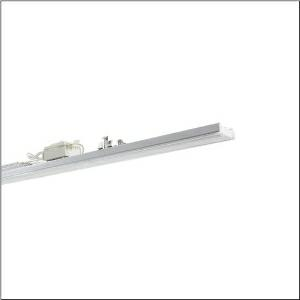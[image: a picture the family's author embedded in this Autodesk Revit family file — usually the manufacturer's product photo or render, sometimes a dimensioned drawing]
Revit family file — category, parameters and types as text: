
# Revit family: licross_r__21_recessed_ho_52tl12mn4fxm_f100
name_source: partatom
category: Lighting Fixtures
units: mm (PartAtom-declared; Revit-internal decimal feet)

## family parameters
Cut with Voids When Loaded = No
Host = Face
Light Source = No
Part Type = Normal
Room Calculation Point = No
Round Connector Dimension = Use Diameter
Shared = No

## types (1)
- --- (1 x LED, 15100 lm, 83.1 W, 4000K)
    Apparent Load = 83 VA
    CIE Flux Codes = 69 91 98 100 100
    Color Rendering = 80
    Color Temperature = 4000K
    Default Elevation = 1800 mm
    Description = Licross® 21 Recessed HO, luminaire insert, of sheet steel, galvanised, coil coated, white, length: 1.500mm, width: 66mm, height: 67mm, LED rated luminous flux: 15.100lm, light colour: 840, control gear: ON/OFF Multilumen, with plug, 3-pole, with phase selection, mains connection: 220..240V, AC, 50/60Hz, rated input power: 83W, halogen-free wiring, primary optical cover: cover, of PMMA, light emission: direct distribution, primary light characteristic: symmetric, protection rating (complete): IP40, insulation class (complete): insulation class I (protective earthing), certification: CE, ENEC, VDE, UKCA, protection symbol: D if used in an environment without relevant dust loads with corresponding accessories, impact resistance: IK06, permissible ambient temperature for indoor applications: -35..+30°C, corresponds to IFS (International Featured Standards) requirements for safety and quality in the food industry, reducing of maximum allowable ambient temperature of 5°C with ceiling mounting, LABS conformity tested according to VDMA 24364:2018-05, packaging unit: 1 piece
    Height = 58 mm
    Lamp = 1 x LED
    Lamp Light Flux = 15100 lm
    Lamp Power = 83.1 W
    Lamp count = 1
    Length = 1500 mm
    Luminous efficacy = 182 lm/W
    Manufacturer = Siteco
    ModVariant = No
    Model = 52TL12MN4FXM
    Mounting Place = Ceiling
    Mounting Type = Pendant
    Number of Poles = 1
    OnlyDefault = Yes
    Power Factor = 1
    Product Name = Licross® 21 Recessed HO
    Product group = luminaire insert
    ProductGroupID = 902
    Protection Class = Protection class I
    Protection Degree = IP 40
    RLX_Detail_Level = 1
    RLX_Emergency_Light_Flux = 0 lm
    RLX_Emergency_Type = 0
    RLX_Emergency_Type_DB = No
    RlxData = <blob elided: 22329 chars, md5=3d23784e>
    Socket = socket
    Standby Power = 0 W
    System Light Flux = 15100 lm
    System Power = 83 W
    Type Comments = factory setting: luminous flux: 100 % | (A | C | E) | 195 mA
    Type Image = l_1296930.jpg
    URL = http://relux.com
    VarID = @adj_103168
    Voltage = 0 V
    Weight = 0.00 kg
    Width = 66 mm

## geometry (parser evidence)
native form markers: Blend x4, Sweep x13
no freeform markers — native parametric forms only
